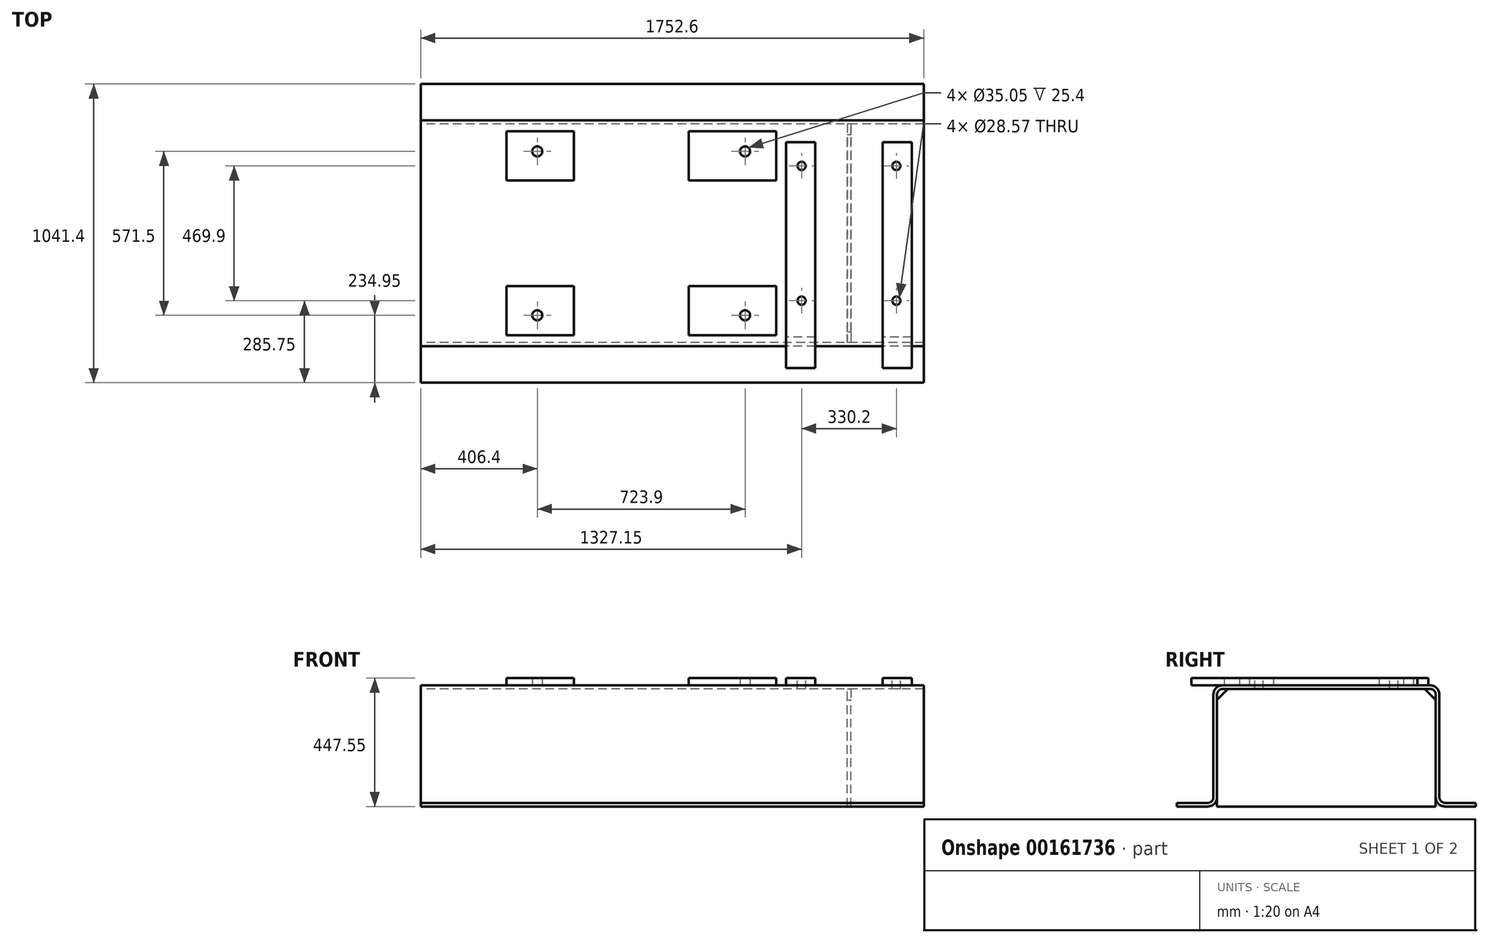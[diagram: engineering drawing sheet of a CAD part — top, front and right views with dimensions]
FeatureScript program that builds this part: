
annotation { "Feature Type Name" : "Feature", "Feature Type Description" : "" }
export const myFeature = defineFeature(function(context is Context, id is Id, definition is map)
    precondition{}
    {
        {
            var Q0;
            Q0=qCreatedBy(makeId("Right.planeOp"),FACE);
            var sketch = newSketch(context, id + "F0", { "sketchPlane" : qUnion([Q0])});
            skLineSegment(sketch, "E0", {"start": v(-520.7, 0) * mm, "end": v(520.7, 0) * mm, "construction": true});
            skLineSegment(sketch, "E1", {"start": v(0, 0) * mm, "end": v(0, 422.15) * mm, "construction": true});
            skLineSegment(sketch, "E2", {"start": v(0, 422.15) * mm, "end": v(361.95, 422.15) * mm});
            skLineSegment(sketch, "E3", {"start": v(393.7, 390.4) * mm, "end": v(393.7, 31.75) * mm});
            skLineSegment(sketch, "E4", {"start": v(412.75, 12.7) * mm, "end": v(520.7, 12.7) * mm});
            skLineSegment(sketch, "E5", {"start": v(520.7, 12.7) * mm, "end": v(520.7, 0) * mm});
            skLineSegment(sketch, "E6", {"start": v(520.7, 0) * mm, "end": v(412.75, 0) * mm});
            skLineSegment(sketch, "E7", {"start": v(381, 31.75) * mm, "end": v(381, 390.4) * mm});
            skLineSegment(sketch, "E8", {"start": v(361.95, 409.45) * mm, "end": v(0, 409.45) * mm});
            skPoint(sketch, "E9.visualSharp", {"position": v(381, 409.45) * mm});
            skArc(sketch, "E9.filletArc", {"start": v(381, 390.4) * mm, "mid": v(375.42, 403.87) * mm, "end": v(361.95, 409.45) * mm});
            skPoint(sketch, "E10.visualSharp", {"position": v(393.7, 12.7) * mm});
            skArc(sketch, "E10.filletArc", {"start": v(393.7, 31.75) * mm, "mid": v(399.28, 18.28) * mm, "end": v(412.75, 12.7) * mm});
            skPoint(sketch, "E11.visualSharp", {"position": v(393.7, 422.15) * mm});
            skArc(sketch, "E11.filletArc", {"start": v(393.7, 390.4) * mm, "mid": v(384.4, 412.85) * mm, "end": v(361.95, 422.15) * mm});
            skPoint(sketch, "E12.visualSharp", {"position": v(381, 0) * mm});
            skArc(sketch, "E12.filletArc", {"start": v(381, 31.75) * mm, "mid": v(390.3, 9.3) * mm, "end": v(412.75, 0) * mm});
            skLineSegment(sketch, "E13.MirrorCS", {"start": v(-520.7, 12.7) * mm, "end": v(-520.7, 0) * mm});
            skArc(sketch, "E14.MirrorCS", {"start": v(-381, 390.4) * mm, "mid": v(-375.42, 403.87) * mm, "end": v(-361.95, 409.45) * mm});
            skArc(sketch, "E15.MirrorCS", {"start": v(-393.7, 31.75) * mm, "mid": v(-399.28, 18.28) * mm, "end": v(-412.75, 12.7) * mm});
            skArc(sketch, "E16.MirrorCS", {"start": v(-381, 31.75) * mm, "mid": v(-390.3, 9.3) * mm, "end": v(-412.75, 0) * mm});
            skArc(sketch, "E17.MirrorCS", {"start": v(-393.7, 390.4) * mm, "mid": v(-384.4, 412.85) * mm, "end": v(-361.95, 422.15) * mm});
            skLineSegment(sketch, "E18.MirrorCS", {"start": v(520.7, 0) * mm, "end": v(-520.7, 0) * mm, "construction": true});
            skPoint(sketch, "E19.MirrorP", {"position": v(-393.7, 422.15) * mm});
            skPoint(sketch, "E20.MirrorP", {"position": v(-381, 409.45) * mm});
            skPoint(sketch, "E21.MirrorP", {"position": v(-393.7, 12.7) * mm});
            skLineSegment(sketch, "E22.MirrorCS", {"start": v(0, 422.15) * mm, "end": v(-361.95, 422.15) * mm});
            skLineSegment(sketch, "E23.MirrorCS", {"start": v(-393.7, 390.4) * mm, "end": v(-393.7, 31.75) * mm});
            skLineSegment(sketch, "E24.MirrorCS", {"start": v(-520.7, 0) * mm, "end": v(-412.75, 0) * mm});
            skLineSegment(sketch, "E25.MirrorCS", {"start": v(-381, 31.75) * mm, "end": v(-381, 390.4) * mm});
            skLineSegment(sketch, "E26.MirrorCS", {"start": v(-361.95, 409.45) * mm, "end": v(0, 409.45) * mm});
            skLineSegment(sketch, "E27.MirrorCS", {"start": v(-412.75, 12.7) * mm, "end": v(-520.7, 12.7) * mm});
            skPoint(sketch, "E28.MirrorP", {"position": v(-381, 0) * mm});
            skSolve(sketch);
        }
        {
            var Q0;
            Q0=qSketchRegion(id+"F0",true);
            extrude(context, id + "F1", {"entities" : qUnion([Q0]), "endBound" : BoundingType.SYMMETRIC, "depth" : 1752.6 * mm});
        }
        {
            var Q0;
            Q0=makeQuery(id+"F1.opExtrude","SWEPT_FACE",FACE,{"disambiguationData":[OSD([sQuery(id+"F0.wireOp",EDGE,"E2"),sQuery(id+"F0.wireOp",EDGE,"E22.MirrorCS")])]});
            var sketch = newSketch(context, id + "F2", { "sketchPlane" : qUnion([Q0])});
            skLineSegment(sketch, "E29.0", {"start": v(-1765.3, -1196.64) * mm, "end": v(-1765.3, 361.95) * mm, "construction": true});
            skLineSegment(sketch, "E30.0", {"start": v(-1257.3, -1196.64) * mm, "end": v(-1257.3, 361.95) * mm, "construction": true});
            skLineSegment(sketch, "E31.0", {"start": v(-107.95, -1196.64) * mm, "end": v(-107.95, 361.95) * mm, "construction": true});
            skLineSegment(sketch, "E32.0", {"start": v(615.95, -1196.64) * mm, "end": v(615.95, 361.95) * mm, "construction": true});
            skLineSegment(sketch, "E33", {"start": v(-1935.84, 0) * mm, "end": v(1124.96, 0) * mm, "construction": true});
            skLineSegment(sketch, "E34.0", {"start": v(-342.9, -1196.64) * mm, "end": v(-342.9, 361.95) * mm, "construction": true});
            skLineSegment(sketch, "E35.0", {"start": v(-577.85, -1196.64) * mm, "end": v(-577.85, 361.95) * mm, "construction": true});
            skLineSegment(sketch, "E36.0", {"start": v(57.15, -1196.64) * mm, "end": v(57.15, 361.95) * mm, "construction": true});
            skLineSegment(sketch, "E37.0", {"start": v(361.95, -1196.64) * mm, "end": v(361.95, 361.95) * mm, "construction": true});
            skLineSegment(sketch, "E38.0", {"start": v(-1935.84, -184.15) * mm, "end": v(1124.96, -184.15) * mm, "construction": true});
            skLineSegment(sketch, "E39.0", {"start": v(-1935.84, -355.6) * mm, "end": v(1124.96, -355.6) * mm, "construction": true});
            skLineSegment(sketch, "E40.bottom", {"start": v(-342.9, -355.6) * mm, "end": v(-577.85, -355.6) * mm});
            skLineSegment(sketch, "E40.top", {"start": v(-342.9, -184.15) * mm, "end": v(-577.85, -184.15) * mm});
            skLineSegment(sketch, "E40.left", {"start": v(-342.9, -355.6) * mm, "end": v(-342.9, -184.15) * mm});
            skLineSegment(sketch, "E40.right", {"start": v(-577.85, -355.6) * mm, "end": v(-577.85, -184.15) * mm});
            skLineSegment(sketch, "E41.bottom", {"start": v(57.15, -184.15) * mm, "end": v(361.95, -184.15) * mm});
            skLineSegment(sketch, "E41.top", {"start": v(57.15, -355.6) * mm, "end": v(361.95, -355.6) * mm});
            skLineSegment(sketch, "E41.left", {"start": v(57.15, -184.15) * mm, "end": v(57.15, -355.6) * mm});
            skLineSegment(sketch, "E41.right", {"start": v(361.95, -184.15) * mm, "end": v(361.95, -355.6) * mm});
            skLineSegment(sketch, "E42.0", {"start": v(-469.9, -1196.64) * mm, "end": v(-469.9, 361.95) * mm, "construction": true});
            skLineSegment(sketch, "E43.0", {"start": v(254, -1196.64) * mm, "end": v(254, 361.95) * mm, "construction": true});
            skLineSegment(sketch, "E44.0", {"start": v(-1935.84, -285.75) * mm, "end": v(1124.96, -285.75) * mm, "construction": true});
            skCircle(sketch, "E45", {"center": v(-469.9, -285.75) * mm, "radius": 17.53 * mm});
            skCircle(sketch, "E46", {"center": v(254, -285.75) * mm, "radius": 17.53 * mm});
            skCircle(sketch, "E47.MirrorC", {"center": v(-469.9, 285.75) * mm, "radius": 17.53 * mm});
            skLineSegment(sketch, "E48.MirrorCS", {"start": v(-342.9, 355.6) * mm, "end": v(-342.9, 184.15) * mm});
            skCircle(sketch, "E49.MirrorC", {"center": v(254, 285.75) * mm, "radius": 17.53 * mm});
            skLineSegment(sketch, "E50.MirrorCS", {"start": v(57.15, 184.15) * mm, "end": v(361.95, 184.15) * mm});
            skLineSegment(sketch, "E51.MirrorCS", {"start": v(-577.85, 355.6) * mm, "end": v(-577.85, 184.15) * mm});
            skLineSegment(sketch, "E52.MirrorCS", {"start": v(57.15, 355.6) * mm, "end": v(361.95, 355.6) * mm});
            skLineSegment(sketch, "E53.MirrorCS", {"start": v(57.15, 184.15) * mm, "end": v(57.15, 355.6) * mm});
            skLineSegment(sketch, "E54.MirrorCS", {"start": v(-342.9, 184.15) * mm, "end": v(-577.85, 184.15) * mm});
            skLineSegment(sketch, "E55.MirrorCS", {"start": v(361.95, 184.15) * mm, "end": v(361.95, 355.6) * mm});
            skLineSegment(sketch, "E56.MirrorCS", {"start": v(-342.9, 355.6) * mm, "end": v(-577.85, 355.6) * mm});
            skSolve(sketch);
        }
        {
            var Q0;
            Q0=qSketchRegion(id+"F2",true);
            extrude(context, id + "F3", {"entities" : qUnion([Q0]), "operationType" : NewBodyOperationType.ADD, "depth" : 25.4 * mm});
        }
        {
            var Q0;
            Q0=makeQuery(id+"F2.imprint","IMPRINT",FACE,{"disambiguationData":[TD([[makeQuery(id+"F2.imprint","IMPRINT",EDGE,{"derivedFrom":sQuery(id+"F2.wireOp",EDGE,"E40.bottom")}),1.0]])]});
            var sketch = newSketch(context, id + "F4", { "sketchPlane" : qUnion([Q0])});
            skLineSegment(sketch, "E57.0", {"start": v(615.95, -1196.64) * mm, "end": v(615.95, 361.95) * mm, "construction": true});
            skLineSegment(sketch, "E58.0", {"start": v(498.6, -1196.64) * mm, "end": v(498.6, 361.95) * mm, "construction": true});
            skLineSegment(sketch, "E59.0", {"start": v(397, -1196.64) * mm, "end": v(397, 361.95) * mm, "construction": true});
            skLineSegment(sketch, "E60.0", {"start": v(-1935.84, 317.5) * mm, "end": v(1124.96, 317.5) * mm, "construction": true});
            skLineSegment(sketch, "E61.bottom", {"start": v(397, 317.5) * mm, "end": v(498.6, 317.5) * mm});
            skLineSegment(sketch, "E61.top", {"start": v(397, -469.9) * mm, "end": v(498.6, -469.9) * mm});
            skLineSegment(sketch, "E61.left", {"start": v(397, 317.5) * mm, "end": v(397, -469.9) * mm});
            skLineSegment(sketch, "E61.right", {"start": v(498.6, 317.5) * mm, "end": v(498.6, -469.9) * mm});
            skLineSegment(sketch, "E62.MirrorCS", {"start": v(834.9, -469.9) * mm, "end": v(733.3, -469.9) * mm});
            skLineSegment(sketch, "E63.MirrorCS", {"start": v(834.9, 317.5) * mm, "end": v(733.3, 317.5) * mm});
            skLineSegment(sketch, "E64.MirrorCS", {"start": v(733.3, 317.5) * mm, "end": v(733.3, -469.9) * mm});
            skLineSegment(sketch, "E65.MirrorCS", {"start": v(834.9, 317.5) * mm, "end": v(834.9, -469.9) * mm});
            skSolve(sketch);
        }
        {
            var Q0;
            Q0=qSketchRegion(id+"F4",true);
            extrude(context, id + "F5", {"entities" : qUnion([Q0]), "operationType" : NewBodyOperationType.ADD, "depth" : 25.4 * mm});
        }
        {
            var Q0;
            Q0=makeQuery(id+"F5.opExtrude","CAP_FACE",FACE,{"disambiguationData":[OSD([sQuery(id+"F4.wireOp",EDGE,"E61.bottom"),sQuery(id+"F4.wireOp",EDGE,"E61.top"),sQuery(id+"F4.wireOp",EDGE,"E61.left"),sQuery(id+"F4.wireOp",EDGE,"E61.right")])],"isStart":false});
            var sketch = newSketch(context, id + "F6", { "sketchPlane" : qUnion([Q0])});
            skLineSegment(sketch, "E66.0", {"start": v(615.95, -1196.64) * mm, "end": v(615.95, 361.95) * mm, "construction": true});
            skLineSegment(sketch, "E67.0", {"start": v(-1935.84, 0) * mm, "end": v(1124.96, 0) * mm, "construction": true});
            skLineSegment(sketch, "E68.0", {"start": v(-1935.84, -234.95) * mm, "end": v(1124.96, -234.95) * mm, "construction": true});
            skLineSegment(sketch, "E69.0", {"start": v(-1935.84, 234.95) * mm, "end": v(1124.96, 234.95) * mm, "construction": true});
            skLineSegment(sketch, "E70.0", {"start": v(450.85, -1196.64) * mm, "end": v(450.85, 361.95) * mm, "construction": true});
            skLineSegment(sketch, "E71.0", {"start": v(781.05, -1196.64) * mm, "end": v(781.05, 361.95) * mm, "construction": true});
            skPoint(sketch, "E72", {"position": v(450.85, 234.95) * mm});
            skPoint(sketch, "E73", {"position": v(781.05, 234.95) * mm});
            skPoint(sketch, "E74", {"position": v(450.85, -234.95) * mm});
            skPoint(sketch, "E75", {"position": v(781.05, -234.95) * mm});
            skSolve(sketch);
        }
        {
            var Q0;
            Q0=sQuery(id+"F6.wireOp",VERTEX,"E72");
            var Q1;
            Q1=sQuery(id+"F6.wireOp",VERTEX,"E73");
            var Q2;
            Q2=sQuery(id+"F6.wireOp",VERTEX,"E74");
            var Q3;
            Q3=sQuery(id+"F6.wireOp",VERTEX,"E75");
            var Q4;
            Q4=makeQuery(id+"F1.opExtrude","SWEPT_BODY",BODY,{"disambiguationData":[OSD([sQuery(id+"F0.wireOp",EDGE,"E2"),sQuery(id+"F0.wireOp",EDGE,"E3"),sQuery(id+"F0.wireOp",EDGE,"E4"),sQuery(id+"F0.wireOp",EDGE,"E5"),sQuery(id+"F0.wireOp",EDGE,"E6"),sQuery(id+"F0.wireOp",EDGE,"E7"),sQuery(id+"F0.wireOp",EDGE,"E8"),sQuery(id+"F0.wireOp",EDGE,"E9.filletArc"),sQuery(id+"F0.wireOp",EDGE,"E10.filletArc"),sQuery(id+"F0.wireOp",EDGE,"E11.filletArc"),sQuery(id+"F0.wireOp",EDGE,"E12.filletArc"),sQuery(id+"F0.wireOp",EDGE,"E13.MirrorCS"),sQuery(id+"F0.wireOp",EDGE,"E14.MirrorCS"),sQuery(id+"F0.wireOp",EDGE,"E15.MirrorCS"),sQuery(id+"F0.wireOp",EDGE,"E16.MirrorCS"),sQuery(id+"F0.wireOp",EDGE,"E17.MirrorCS"),sQuery(id+"F0.wireOp",EDGE,"E22.MirrorCS"),sQuery(id+"F0.wireOp",EDGE,"E23.MirrorCS"),sQuery(id+"F0.wireOp",EDGE,"E24.MirrorCS"),sQuery(id+"F0.wireOp",EDGE,"E25.MirrorCS"),sQuery(id+"F0.wireOp",EDGE,"E26.MirrorCS"),sQuery(id+"F0.wireOp",EDGE,"E27.MirrorCS")])]});
            hole(context, id + "F7", {"style" : HoleStyle.SIMPLE, "holeDiameter" : 28.57 * mm, "endStyle" : HoleEndStyle.THROUGH, "locations" : qUnion([Q0, Q1, Q2, Q3]), "scope" : qUnion([Q4])});
        }
        {
            var Q0;
            Q0=makeQuery(id+"F1.opExtrude","SWEPT_FACE",FACE,{"disambiguationData":[OSD([sQuery(id+"F0.wireOp",EDGE,"E8"),sQuery(id+"F0.wireOp",EDGE,"E26.MirrorCS")])]});
            var sketch = newSketch(context, id + "F8", { "sketchPlane" : qUnion([Q0])});
            skLineSegment(sketch, "E76.0", {"start": v(615.95, 381) * mm, "end": v(615.95, -381) * mm, "construction": true});
            skLineSegment(sketch, "E77.0.1", {"start": v(-876.3, -381) * mm, "end": v(876.3, -381) * mm, "construction": true});
            skLineSegment(sketch, "E77.0.3", {"start": v(876.3, -381) * mm, "end": v(-876.3, -381) * mm, "construction": true});
            skLineSegment(sketch, "E78.0.1", {"start": v(-876.3, 381) * mm, "end": v(876.3, 381) * mm, "construction": true});
            skLineSegment(sketch, "E78.0.3", {"start": v(876.3, 381) * mm, "end": v(-876.3, 381) * mm, "construction": true});
            skPoint(sketch, "E79.orphan", {"position": v(615.95, -361.95) * mm});
            skPoint(sketch, "E80.orphan", {"position": v(615.95, 1196.64) * mm});
            skLineSegment(sketch, "E81.0", {"start": v(609.6, 381) * mm, "end": v(609.6, -381) * mm});
            skLineSegment(sketch, "E82.bottom", {"start": v(609.6, 381) * mm, "end": v(622.3, 381) * mm});
            skLineSegment(sketch, "E82.top", {"start": v(609.6, -381) * mm, "end": v(622.3, -381) * mm});
            skLineSegment(sketch, "E82.right", {"start": v(622.3, 381) * mm, "end": v(622.3, -381) * mm});
            skSolve(sketch);
        }
        {
            var Q0;
            Q0=qSketchRegion(id+"F8",true);
            var Q1;
            Q1=makeQuery(id+"F1.opExtrude","SWEPT_FACE",FACE,{"disambiguationData":[OSD([sQuery(id+"F0.wireOp",EDGE,"E24.MirrorCS")])]});
            extrude(context, id + "F9", {"entities" : qUnion([Q0]), "endBound" : BoundingType.UP_TO_SURFACE, "endBoundEntityFace" : qUnion([Q1]), "depth" : 25.4 * mm});
        }
        {
            var Q0;
            Q0=makeQuery(id+"F9.opExtrude","CAP_EDGE",EDGE,{"disambiguationData":[OSD([sQuery(id+"F8.wireOp",EDGE,"E82.top")])],"isStart":true});
            var Q1;
            Q1=makeQuery(id+"F9.opExtrude","CAP_EDGE",EDGE,{"disambiguationData":[OSD([sQuery(id+"F8.wireOp",EDGE,"E82.bottom")])],"isStart":true});
            chamfer(context, id + "F10", {"entities" : qUnion([Q0, Q1]), "width" : 38.1 * mm, "tangentPropagation" : true});
        }
    });
